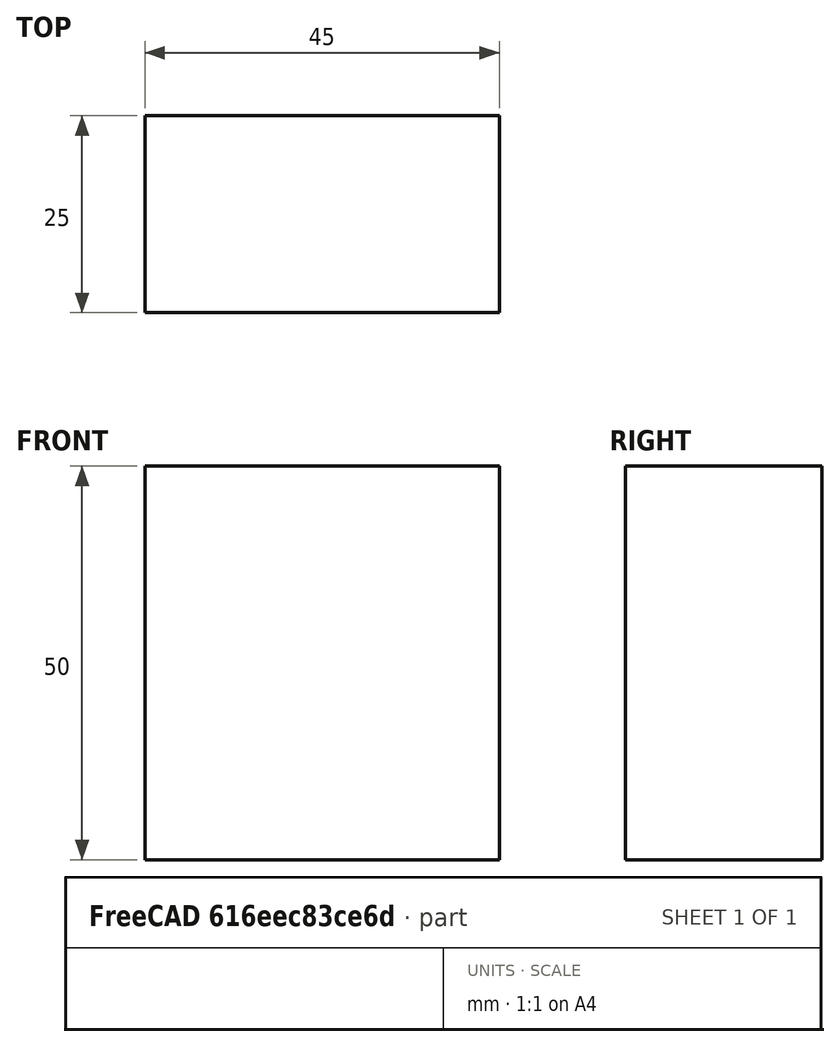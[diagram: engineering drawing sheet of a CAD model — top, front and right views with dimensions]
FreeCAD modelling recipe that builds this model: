
FCSTD DOCUMENT  (FreeCAD 0.15R4671 (Git))
Label: Flat Bar 45x25 EN10058 S235JR
License: All rights reserved
LicenseURL: http://en.wikipedia.org/wiki/All_rights_reserved
objects: Sketcher::SketchObject×1, Part::Extrusion×1
note: 2 computed .brp shape members not serialized (recipe doc carries the construction recipe); baked Part::Feature solids carry a one-line shape summary decoded from their .brp

FEATURE [Sketcher::SketchObject] Sketch
  sketch-geometry (4):
    g0: LineSegment StartX=-22.5 StartY=-12.5 StartZ=0 EndX=22.5 EndY=-12.5 EndZ=0
    g1: LineSegment StartX=22.5 StartY=-12.5 StartZ=0 EndX=22.5 EndY=12.5 EndZ=0
    g2: LineSegment StartX=22.5 StartY=12.5 StartZ=0 EndX=-22.5 EndY=12.5 EndZ=0
    g3: LineSegment StartX=-22.5 StartY=12.5 StartZ=0 EndX=-22.5 EndY=-12.5 EndZ=0
  constraints (12):
    c: Coincident(g0,g1)
    c: Coincident(g1,g2)
    c: Coincident(g2,g3)
    c: Coincident(g3,g0)
    c: Horizontal(g0)
    c: Horizontal(g2)
    c: Vertical(g1)
    c: Vertical(g3)
    c: Symmetric(g1,g2,g-2)
    c: Symmetric(g0,g1,g-1)
    c: DistanceY(g1) = 25
    c: DistanceX(g0) = 45
FEATURE [Part::Extrusion] Extrude  label="Flat Bar 45x25 EN10058 S235JR"
  Base = -> Sketch
  Dir = (0,0,50)
  Solid = true
